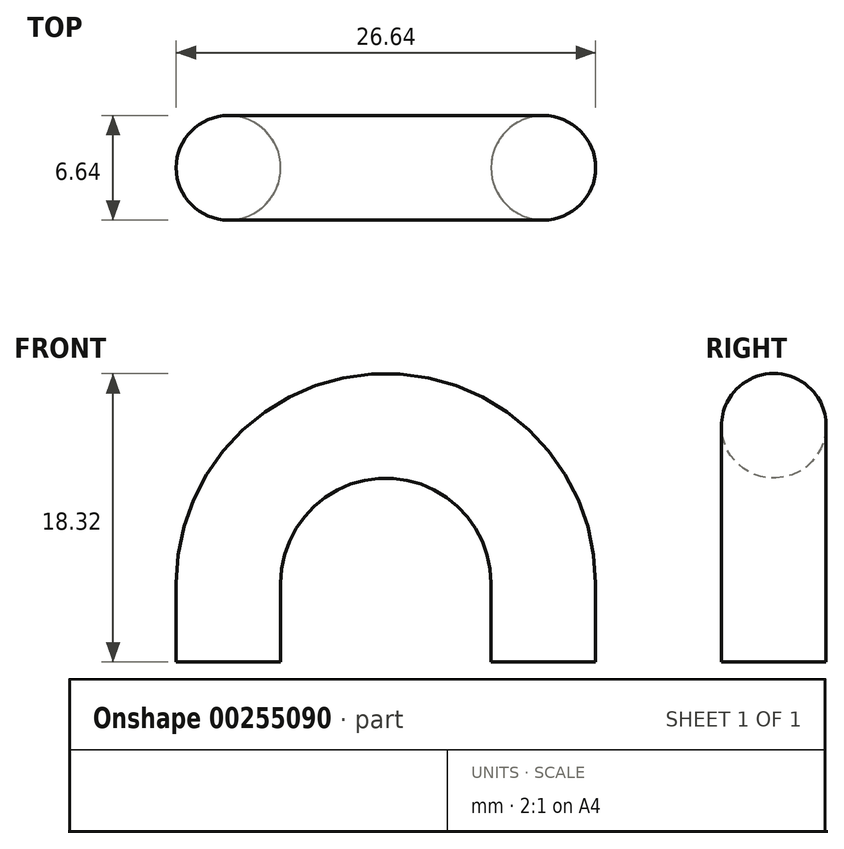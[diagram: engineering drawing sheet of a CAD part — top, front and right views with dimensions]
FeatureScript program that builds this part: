
annotation { "Feature Type Name" : "Feature", "Feature Type Description" : "" }
export const myFeature = defineFeature(function(context is Context, id is Id, definition is map)
    precondition{}
    {
        {
            var Q0;
            Q0=qCreatedBy(makeId("Front.planeOp"),FACE);
            var sketch = newSketch(context, id + "F0", { "sketchPlane" : qUnion([Q0])});
            skLineSegment(sketch, "E0", {"start": v(10, 0) * mm, "end": v(10, 5) * mm});
            skArc(sketch, "E1", {"start": v(10, 5) * mm, "mid": v(0, 15) * mm, "end": v(-10, 5) * mm});
            skLineSegment(sketch, "E2", {"start": v(-10, 5) * mm, "end": v(-10, 0) * mm});
            skSolve(sketch);
        }
        {
            var Q0;
            Q0=qCreatedBy(makeId("Top.planeOp"),FACE);
            var sketch = newSketch(context, id + "F1", { "sketchPlane" : qUnion([Q0])});
            skCircle(sketch, "E3", {"center": v(10, 0) * mm, "radius": 3.32 * mm});
            skSolve(sketch);
        }
        {
            var Q0;
            Q0=makeQuery(id+"F1.imprint","IMPRINT",FACE,{"disambiguationData":[TD([[makeQuery(id+"F1.imprint","IMPRINT",EDGE,{"derivedFrom":sQuery(id+"F1.wireOp",EDGE,"E3")}),1.0]])]});
            var Q1;
            Q1 = qConstructionFilter(qBodyType(qCreatedBy(id + "F0" ,EDGE), BodyType.WIRE), ConstructionObject.NO);
            sweep(context, id + "F2", {"profiles" : qUnion([Q0]), "path" : qUnion([Q1])});
        }
    });
